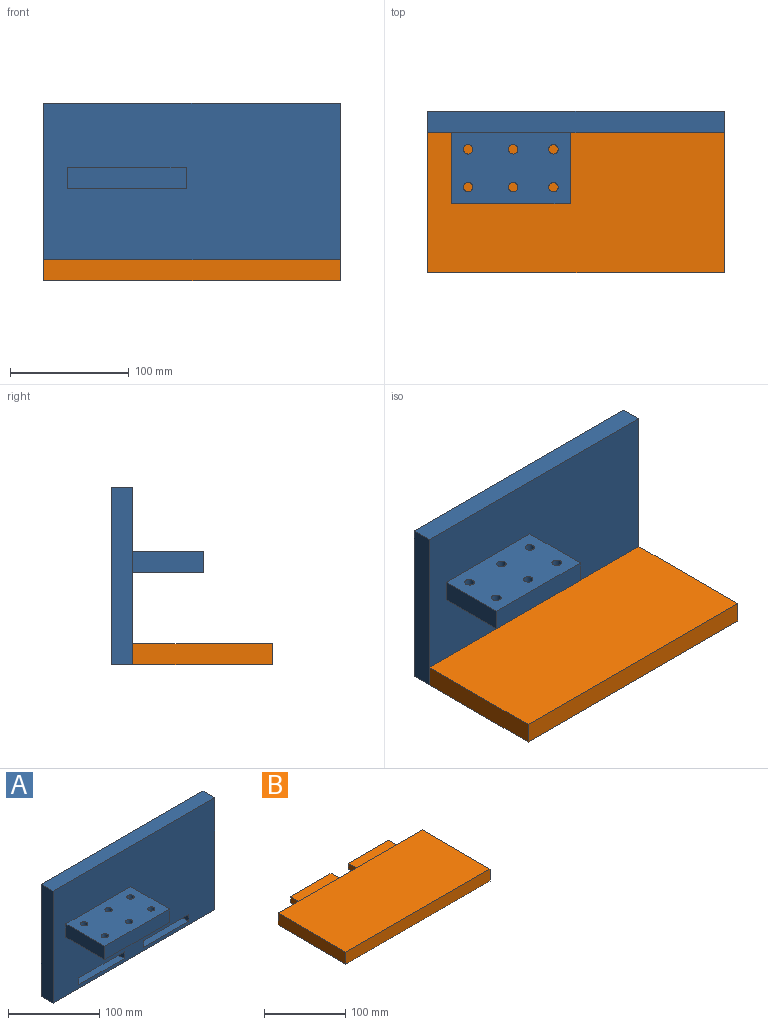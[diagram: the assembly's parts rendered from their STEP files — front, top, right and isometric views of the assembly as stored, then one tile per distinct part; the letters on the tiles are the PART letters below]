
ASSEMBLY  parts=2 mates=1
PART A: 25 faces, bbox 250x78x150 mm
  f0: plane 250x150mm, normal (0,-1,0), area 34440mm2, adj f2,f3,f4,f5,f6,f7,f8,f9
  f1: plane 250x150mm, normal (0,1,0), area 36240mm2, adj f2,f3,f4,f5,f6,f7,f8,f9
  f2: plane 250x18mm, normal (0,0,1), area 4500mm2, adj f0,f1,f3,f5
  f3: plane 150x18mm, normal (-1,0,0), area 2700mm2, adj f0,f1,f2,f4
  f4: plane 250x18mm, normal (0,0,-1), area 4500mm2, adj f0,f1,f3,f5
  f5: plane 150x18mm, normal (1,0,0), area 2700mm2, adj f0,f1,f2,f4
  f6: plane 18x9mm, normal (1,0,0), area 162mm2, adj f0,f1,f7,f9
  f7: plane 70x18mm, normal (0,0,1), area 1260mm2, adj f0,f1,f6,f8
  f8: plane 18x9mm, normal (-1,0,0), area 162mm2, adj f0,f1,f7,f9
  f9: plane 70x18mm, normal (0,0,-1), area 1260mm2, adj f0,f1,f6,f8
  f10: plane 18x9mm, normal (1,0,0), area 162mm2, adj f0,f1,f11,f13
  f11: plane 70x18mm, normal (0,0,1), area 1260mm2, adj f0,f1,f10,f12
  f12: plane 18x9mm, normal (-1,0,0), area 162mm2, adj f0,f1,f11,f13
  f13: plane 70x18mm, normal (0,0,-1), area 1260mm2, adj f0,f1,f10,f12
  f14: plane 100x60mm, normal (0,0,1), area 5698.4mm2, adj f0,f15,f17,f18,f19,f20,f21,f22
  f15: plane 60x18mm, normal (-1,0,0), area 1080mm2, adj f0,f14,f16,f18
  f16: plane 100x60mm, normal (0,0,-1), area 5698.4mm2, adj f0,f15,f17,f18,f19,f20,f21,f22
  f17: plane 60x18mm, normal (1,0,0), area 1080mm2, adj f0,f14,f16,f18
  f18: plane 100x18mm, normal (0,-1,0), area 1800mm2, adj f14,f15,f16,f17
  f19: cylinder r=4mm len=18mm, axis (0,0,1), area 452.4mm2, adj f14,f16
  f20: cylinder r=4mm len=18mm, axis (0,0,1), area 452.4mm2, adj f14,f16
  f21: cylinder r=4mm len=18mm, axis (0,0,1), area 452.4mm2, adj f14,f16
  f22: cylinder r=4mm len=18mm, axis (0,0,1), area 452.4mm2, adj f14,f16
  f23: cylinder r=4mm len=18mm, axis (0,0,1), area 452.4mm2, adj f14,f16
  f24: cylinder r=4mm len=18mm, axis (0,0,1), area 452.4mm2, adj f14,f16
PART B: 16 faces, bbox 250x136x18 mm
  f0: plane 250x118mm, normal (0,0,1), area 29500mm2, adj f1,f3,f4,f5
  f1: plane 118x18mm, normal (-1,0,0), area 2124mm2, adj f0,f2,f4,f5
  f2: plane 250x118mm, normal (0,0,-1), area 29500mm2, adj f1,f3,f4,f5
  f3: plane 118x18mm, normal (1,0,0), area 2124mm2, adj f0,f2,f4,f5
  f4: plane 250x18mm, normal (0,-1,0), area 4500mm2, adj f0,f1,f2,f3
  f5: plane 250x18mm, normal (0,1,0), area 3240mm2, adj f0,f1,f2,f3,f6,f7,f8,f9
  f6: plane 70x18mm, normal (0,0,1), area 1260mm2, adj f5,f7,f9,f10
  f7: plane 18x9mm, normal (1,0,0), area 162mm2, adj f5,f6,f8,f10
  f8: plane 70x18mm, normal (0,0,-1), area 1260mm2, adj f5,f7,f9,f10
  f9: plane 18x9mm, normal (-1,0,0), area 162mm2, adj f5,f6,f8,f10
  f10: plane 70x9mm, normal (0,1,0), area 630mm2, adj f6,f7,f8,f9
  f11: plane 70x18mm, normal (0,0,1), area 1260mm2, adj f5,f12,f14,f15
  f12: plane 18x9mm, normal (1,0,0), area 162mm2, adj f5,f11,f13,f15
  f13: plane 70x18mm, normal (0,0,-1), area 1260mm2, adj f5,f12,f14,f15
  f14: plane 18x9mm, normal (-1,0,0), area 162mm2, adj f5,f11,f13,f15
  f15: plane 70x9mm, normal (0,1,0), area 630mm2, adj f11,f12,f13,f14
PLACE A at identity
PLACE B t=(21.51,-18,-76.74)mm
MATE fastened B.f14 <-> A.f10  axis (-1,0,0) through (-69.19,-9,-86.71)mm
